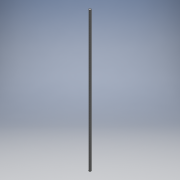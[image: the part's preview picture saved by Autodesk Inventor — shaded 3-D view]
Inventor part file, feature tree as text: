
AUTODESK INVENTOR PART (.ipt)
format: ipt  version: 2018 (Build 220112000, 112)  size: 93,184 bytes
history: native  units: mm
features: sketch x2, extrude x1, thread x1
ambient origin geometry x8: Origin, YZ Plane, XZ Plane, XY Plane, X Axis, Y Axis, Z Axis, Center Point
bodies: Solid1 (feature_tree)
feature tree (4):
  sketch  "Sketch1"  dims[d0=6.0mm d1=393.0mm d2=0.0mm d3=10.0mm d4=0.0mm]
  extrude  "Extrusion1"  Depth=393.0mm TaperAngle=0.0deg
  thread  "Thread1"  [1 undecoded]
  sketch  "Sketch2"
note: 1 required parameter value undecoded (feature->parameter linkage not recoverable at this tier; creation-order binding heuristic only, values carry confidence <= 0.55)
